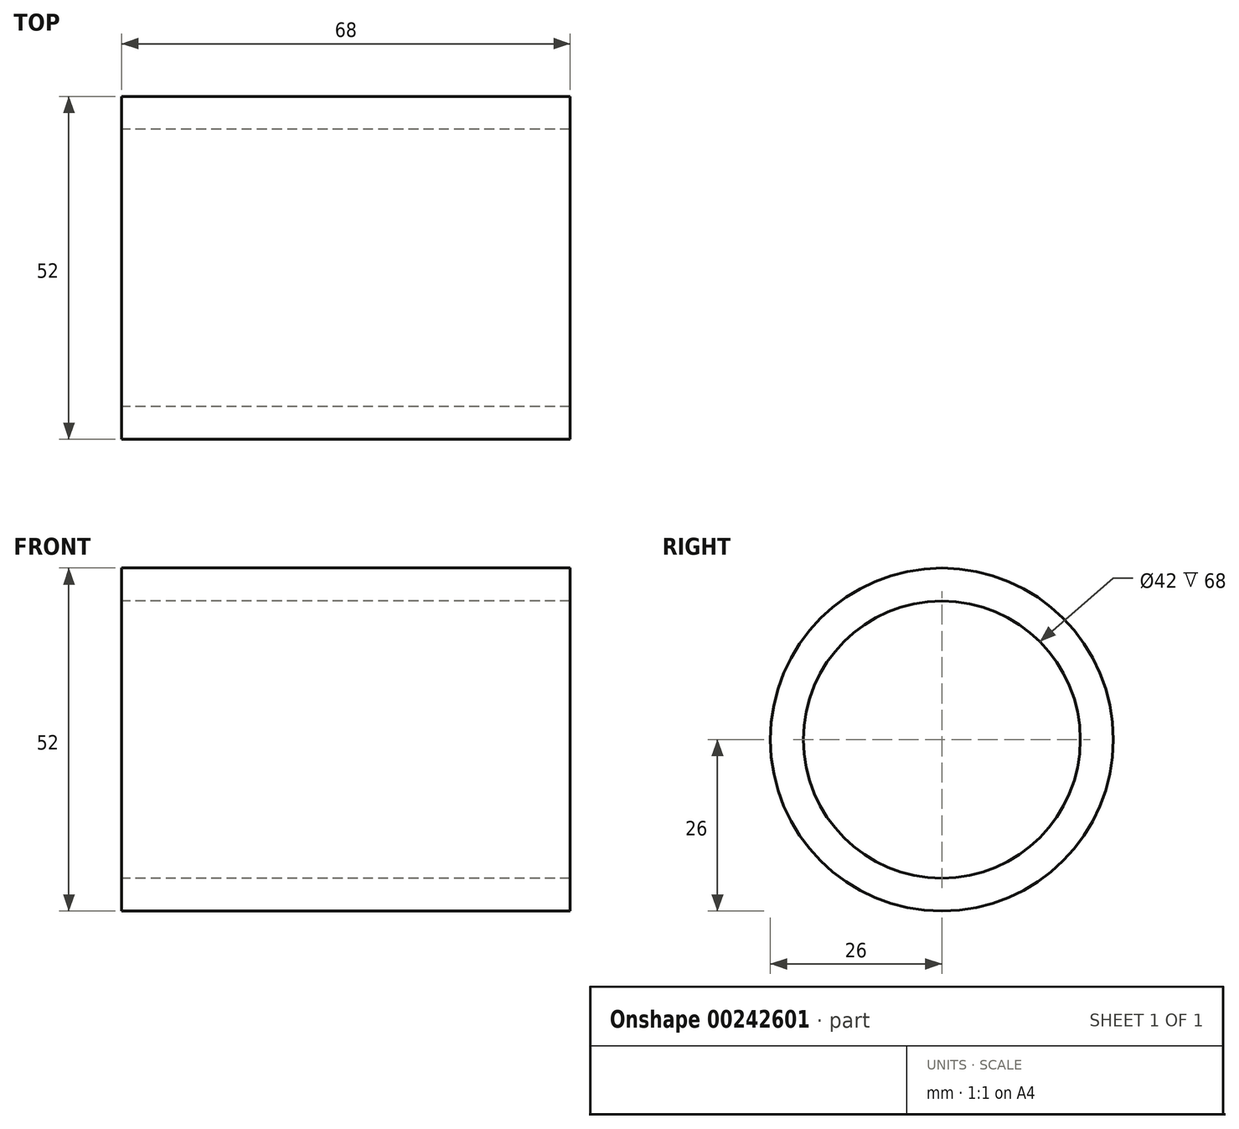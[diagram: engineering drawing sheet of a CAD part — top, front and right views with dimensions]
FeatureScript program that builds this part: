
annotation { "Feature Type Name" : "Feature", "Feature Type Description" : "" }
export const myFeature = defineFeature(function(context is Context, id is Id, definition is map)
    precondition{}
    {
        {
            var Q0;
            Q0=qCreatedBy(makeId("Front.planeOp"),FACE);
            var sketch = newSketch(context, id + "F0", { "sketchPlane" : qUnion([Q0])});
            skLineSegment(sketch, "E0.bottom", {"start": v(-32.35, 0) * mm, "end": v(34.84, 0) * mm, "construction": true});
            skLineSegment(sketch, "E0.left", {"start": v(-32.35, 0) * mm, "end": v(-32.35, 0) * mm});
            skLineSegment(sketch, "E0.right", {"start": v(34.84, 0) * mm, "end": v(34.84, 0) * mm});
            skLineSegment(sketch, "E1.bottom", {"start": v(-34, 21) * mm, "end": v(34, 21) * mm});
            skLineSegment(sketch, "E1.top", {"start": v(-34, 26) * mm, "end": v(34, 26) * mm});
            skLineSegment(sketch, "E1.left", {"start": v(-34, 21) * mm, "end": v(-34, 26) * mm});
            skLineSegment(sketch, "E1.right", {"start": v(34, 21) * mm, "end": v(34, 26) * mm});
            skLineSegment(sketch, "E2", {"start": v(0, -15.57) * mm, "end": v(0, 41.16) * mm, "construction": true});
            skSolve(sketch);
        }
        {
            var Q0;
            Q0=makeQuery(id+"F0.imprint","IMPRINT",FACE,{"disambiguationData":[TD([[makeQuery(id+"F0.imprint","IMPRINT",EDGE,{"derivedFrom":sQuery(id+"F0.wireOp",EDGE,"E1.bottom")}),1.0]])]});
            var Q1;
            Q1=sQuery(id+"F0.wireOp",EDGE,"E0.bottom");
            revolve(context, id + "F1", {"entities" : qUnion([Q0]), "axis" : qUnion([Q1]), "revolveType" : RevolveType.FULL});
        }
    });
